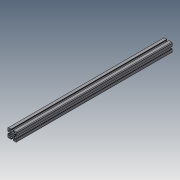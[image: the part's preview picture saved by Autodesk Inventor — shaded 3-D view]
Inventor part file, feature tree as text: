
AUTODESK INVENTOR PART (.ipt)
format: ipt  version: 2018.3 (Build 223284000, 284)  size: 237,568 bytes
history: native  units: in
note: dims shown in document units (in); Inventor stores cm internally (conversion verified against a paired STEP export)
features: extrude x1, sketch x1, projected_geometry x1
ambient origin geometry x8: Origin, YZ Plane, XZ Plane, XY Plane, X Axis, Y Axis, Z Axis, Center Point
bodies: Body1 (feature_tree)
feature tree (3):
  extrude  "Extrusion1"  [1 undecoded]
  sketch  "Sketch1"  dims[d0=27.425in d1=0.0in]
  projected_geometry  "Projected Loop1"
note: 1 required parameter value undecoded (feature->parameter linkage not recoverable at this tier; creation-order binding heuristic only, values carry confidence <= 0.55)
